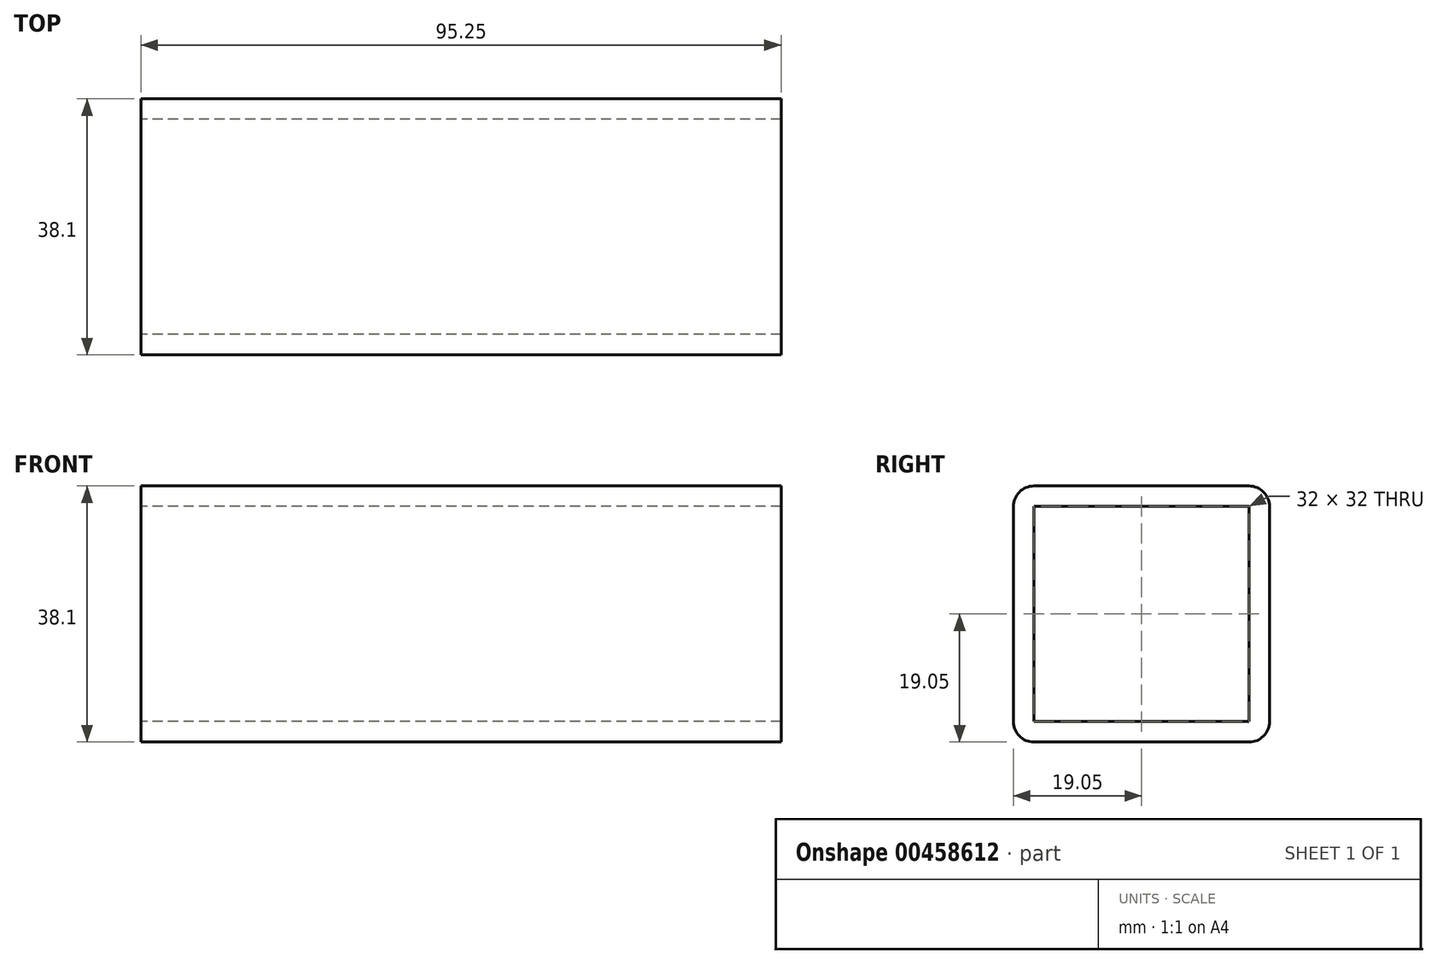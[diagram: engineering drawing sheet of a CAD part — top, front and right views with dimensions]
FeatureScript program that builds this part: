
annotation { "Feature Type Name" : "Feature", "Feature Type Description" : "" }
export const myFeature = defineFeature(function(context is Context, id is Id, definition is map)
    precondition{}
    {
        {
            var Q0;
            Q0=qCreatedBy(makeId("Right.planeOp"),FACE);
            var sketch = newSketch(context, id + "F0", { "sketchPlane" : qUnion([Q0])});
            skLineSegment(sketch, "E0.bottom", {"start": v(16, 19.05) * mm, "end": v(-16, 19.05) * mm});
            skLineSegment(sketch, "E0.top", {"start": v(16, -19.05) * mm, "end": v(-16, -19.05) * mm});
            skLineSegment(sketch, "E0.left", {"start": v(19.05, 16) * mm, "end": v(19.05, -16) * mm});
            skLineSegment(sketch, "E0.right", {"start": v(-19.05, 16) * mm, "end": v(-19.05, -16) * mm});
            skPoint(sketch, "E0.middle", {"position": v(0, 0) * mm});
            skPoint(sketch, "E1.visualSharp", {"position": v(-19.05, 19.05) * mm});
            skArc(sketch, "E1.filletArc", {"start": v(-16, 19.05) * mm, "mid": v(-18.16, 18.16) * mm, "end": v(-19.05, 16) * mm});
            skPoint(sketch, "E2.visualSharp", {"position": v(19.05, 19.05) * mm});
            skArc(sketch, "E2.filletArc", {"start": v(19.05, 16) * mm, "mid": v(18.16, 18.16) * mm, "end": v(16, 19.05) * mm});
            skPoint(sketch, "E3.visualSharp", {"position": v(19.05, -19.05) * mm});
            skArc(sketch, "E3.filletArc", {"start": v(16, -19.05) * mm, "mid": v(18.16, -18.16) * mm, "end": v(19.05, -16) * mm});
            skPoint(sketch, "E4.visualSharp", {"position": v(-19.05, -19.05) * mm});
            skArc(sketch, "E4.filletArc", {"start": v(-19.05, -16) * mm, "mid": v(-18.16, -18.16) * mm, "end": v(-16, -19.05) * mm});
            skLineSegment(sketch, "E5.bottom", {"start": v(16, 16) * mm, "end": v(-16, 16) * mm});
            skLineSegment(sketch, "E5.top", {"start": v(16, -16) * mm, "end": v(-16, -16) * mm});
            skLineSegment(sketch, "E5.left", {"start": v(16, 16) * mm, "end": v(16, -16) * mm});
            skLineSegment(sketch, "E5.right", {"start": v(-16, 16) * mm, "end": v(-16, -16) * mm});
            skSolve(sketch);
        }
        {
            var Q0;
            Q0=makeQuery(id+"F0.imprint","IMPRINT",FACE,{"disambiguationData":[TD([[makeQuery(id+"F0.imprint","IMPRINT",EDGE,{"derivedFrom":sQuery(id+"F0.wireOp",EDGE,"E0.bottom")}),1.0]])]});
            extrude(context, id + "F1", {"entities" : qUnion([Q0]), "depth" : 95.25 * mm});
        }
    });
